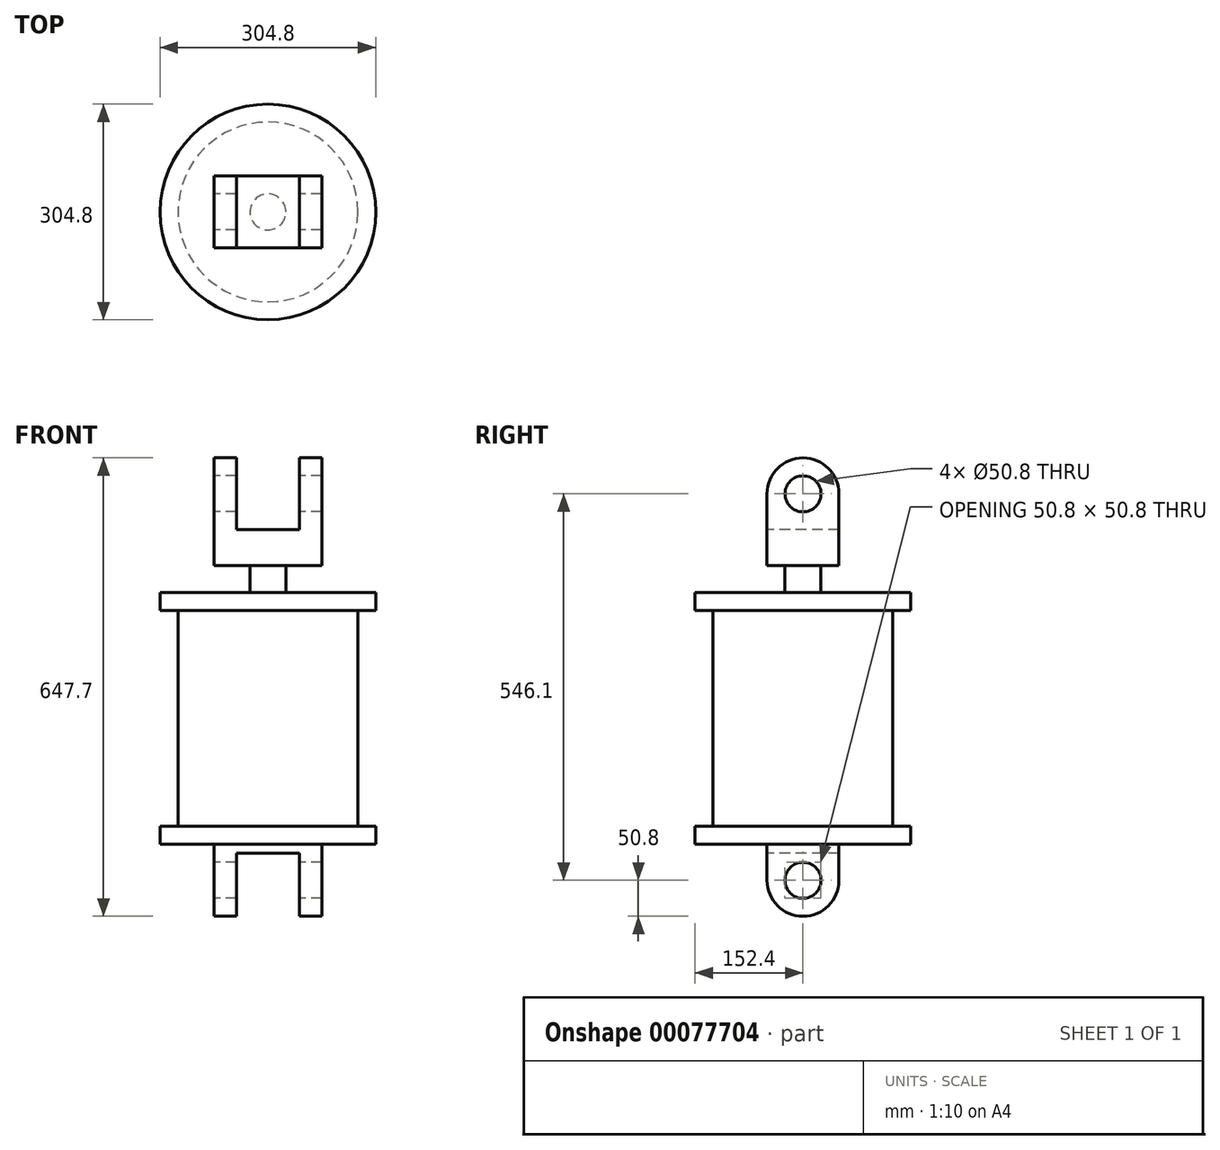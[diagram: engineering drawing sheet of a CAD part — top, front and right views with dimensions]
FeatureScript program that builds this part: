
annotation { "Feature Type Name" : "Feature", "Feature Type Description" : "" }
export const myFeature = defineFeature(function(context is Context, id is Id, definition is map)
    precondition{}
    {
        {
            var Q0;
            Q0=qCreatedBy(makeId("Right.planeOp"),FACE);
            var sketch = newSketch(context, id + "F0", { "sketchPlane" : qUnion([Q0])});
            skCircle(sketch, "E0", {"center": v(0, 0) * mm, "radius": 25.4 * mm});
            skArc(sketch, "E1", {"start": v(-50.8, 0) * mm, "mid": v(0, -50.8) * mm, "end": v(50.8, 0) * mm});
            skLineSegment(sketch, "E2", {"start": v(-50.8, 0) * mm, "end": v(-50.8, 50.8) * mm});
            skLineSegment(sketch, "E3", {"start": v(-50.8, 50.8) * mm, "end": v(50.8, 50.8) * mm});
            skLineSegment(sketch, "E4", {"start": v(50.8, 50.8) * mm, "end": v(50.8, 0) * mm});
            skSolve(sketch);
        }
        {
            var Q0;
            Q0=qSketchRegion(id+"F0",true);
            extrude(context, id + "F1", {"entities" : qUnion([Q0]), "endBound" : BoundingType.SYMMETRIC, "depth" : 152.4 * mm});
        }
        {
            var Q0;
            Q0=makeQuery(id+"F1.opExtrude","SWEPT_FACE",FACE,{"disambiguationData":[OSD([sQuery(id+"F0.wireOp",EDGE,"E2")])]});
            var sketch = newSketch(context, id + "F2", { "sketchPlane" : qUnion([Q0])});
            skLineSegment(sketch, "E5.bottom", {"start": v(-44.45, 38.1) * mm, "end": v(44.45, 38.1) * mm});
            skLineSegment(sketch, "E5.top", {"start": v(-44.45, -62.27) * mm, "end": v(44.45, -62.27) * mm});
            skLineSegment(sketch, "E5.left", {"start": v(-44.45, 38.1) * mm, "end": v(-44.45, -62.27) * mm});
            skLineSegment(sketch, "E5.right", {"start": v(44.45, 38.1) * mm, "end": v(44.45, -62.27) * mm});
            skLineSegment(sketch, "E6", {"start": v(0, 50.8) * mm, "end": v(0, -95.86) * mm, "construction": true});
            skSolve(sketch);
        }
        {
            var Q0;
            Q0=qSketchRegion(id+"F2",true);
            extrude(context, id + "F3", {"entities" : qUnion([Q0]), "operationType" : NewBodyOperationType.REMOVE, "endBound" : BoundingType.THROUGH_ALL, "oppositeDirection" : true, "depth" : 25.4 * mm});
        }
        {
            var Q0;
            Q0=makeQuery(id+"F1.opExtrude","SWEPT_FACE",FACE,{"disambiguationData":[OSD([sQuery(id+"F0.wireOp",EDGE,"E3")])]});
            var sketch = newSketch(context, id + "F4", { "sketchPlane" : qUnion([Q0])});
            skCircle(sketch, "E7", {"center": v(0, 0) * mm, "radius": 152.4 * mm});
            skSolve(sketch);
        }
        {
            var Q0;
            Q0=qSketchRegion(id+"F4",true);
            extrude(context, id + "F5", {"entities" : qUnion([Q0]), "operationType" : NewBodyOperationType.ADD, "depth" : 25.4 * mm});
        }
        {
            var Q0;
            Q0=makeQuery(id+"F5.opExtrude","CAP_FACE",FACE,{"disambiguationData":[OSD([sQuery(id+"F4.wireOp",EDGE,"E7")])],"isStart":false});
            var sketch = newSketch(context, id + "F6", { "sketchPlane" : qUnion([Q0])});
            skCircle(sketch, "E8", {"center": v(0, 0) * mm, "radius": 127 * mm});
            skSolve(sketch);
        }
        {
            var Q0;
            Q0=qSketchRegion(id+"F6",true);
            extrude(context, id + "F7", {"entities" : qUnion([Q0]), "operationType" : NewBodyOperationType.ADD, "depth" : 304.8 * mm});
        }
        {
            var Q0;
            Q0=makeQuery(id+"F7.opExtrude","CAP_FACE",FACE,{"disambiguationData":[OSD([sQuery(id+"F6.wireOp",EDGE,"E8")])],"isStart":false});
            var sketch = newSketch(context, id + "F8", { "sketchPlane" : qUnion([Q0])});
            skCircle(sketch, "E9.0", {"center": v(0, 0) * mm, "radius": 152.4 * mm});
            skSolve(sketch);
        }
        {
            var Q0;
            Q0=qSketchRegion(id+"F8",true);
            extrude(context, id + "F9", {"entities" : qUnion([Q0]), "operationType" : NewBodyOperationType.ADD, "depth" : 25.4 * mm});
        }
        {
            var Q0;
            Q0=makeQuery(id+"F9.opExtrude","CAP_FACE",FACE,{"disambiguationData":[OSD([sQuery(id+"F8.wireOp",EDGE,"E9.0")])],"isStart":false});
            var sketch = newSketch(context, id + "F10", { "sketchPlane" : qUnion([Q0])});
            skCircle(sketch, "E10", {"center": v(0, 0) * mm, "radius": 25.4 * mm});
            skSolve(sketch);
        }
        {
            var Q0;
            Q0=qSketchRegion(id+"F10",true);
            extrude(context, id + "F11", {"entities" : qUnion([Q0]), "operationType" : NewBodyOperationType.ADD, "depth" : 38.1 * mm});
        }
        {
            var Q0;
            Q0=makeQuery(id+"F11.opExtrude","CAP_FACE",FACE,{"disambiguationData":[OSD([sQuery(id+"F10.wireOp",EDGE,"E10")])],"isStart":false});
            var sketch = newSketch(context, id + "F12", { "sketchPlane" : qUnion([Q0])});
            skLineSegment(sketch, "E11.0", {"start": v(76.2, 50.8) * mm, "end": v(-76.2, 50.8) * mm});
            skLineSegment(sketch, "E12.0", {"start": v(76.2, -50.8) * mm, "end": v(76.2, 50.8) * mm});
            skLineSegment(sketch, "E13.0", {"start": v(76.2, -50.8) * mm, "end": v(-76.2, -50.8) * mm});
            skLineSegment(sketch, "E14.0", {"start": v(-76.2, -50.8) * mm, "end": v(-76.2, 50.8) * mm});
            skSolve(sketch);
        }
        {
            var Q0;
            Q0=qSketchRegion(id+"F12",true);
            extrude(context, id + "F13", {"entities" : qUnion([Q0]), "operationType" : NewBodyOperationType.ADD, "depth" : 152.4 * mm});
        }
        {
            var Q0;
            Q0=makeQuery(id+"F13.opExtrude","SWEPT_FACE",FACE,{"disambiguationData":[OSD([sQuery(id+"F12.wireOp",EDGE,"E13.0")])]});
            var sketch = newSketch(context, id + "F14", { "sketchPlane" : qUnion([Q0])});
            skLineSegment(sketch, "E15.0", {"start": v(-44.45, 769.4) * mm, "end": v(-44.45, 495.3) * mm});
            skLineSegment(sketch, "E16.0", {"start": v(44.45, 777.53) * mm, "end": v(44.45, 495.3) * mm});
            skPoint(sketch, "E17.orphan", {"position": v(-44.45, 38.1) * mm});
            skPoint(sketch, "E18.orphan", {"position": v(44.45, 38.1) * mm});
            skLineSegment(sketch, "E19.0", {"start": v(44.45, 495.3) * mm, "end": v(-44.45, 495.3) * mm});
            skLineSegment(sketch, "E20.trimOffspring", {"start": v(-44.45, 38.1) * mm, "end": v(-44.45, 0) * mm});
            skLineSegment(sketch, "E21.trimOffspring", {"start": v(44.45, 38.1) * mm, "end": v(44.45, 0) * mm});
            skLineSegment(sketch, "E22", {"start": v(-44.45, 769.4) * mm, "end": v(44.45, 777.53) * mm});
            skSolve(sketch);
        }
        {
            var Q0;
            Q0=qSketchRegion(id+"F14",true);
            extrude(context, id + "F15", {"entities" : qUnion([Q0]), "operationType" : NewBodyOperationType.REMOVE, "endBound" : BoundingType.THROUGH_ALL, "oppositeDirection" : true, "depth" : 25.4 * mm});
        }
        {
            var Q0;
            {var subQ0=sQuery(id+"F12.wireOp",EDGE,"E11.0");var subQ1=sQuery(id+"F12.wireOp",EDGE,"E14.0");Q0=makeQuery(id+"F15.boolean.opBoolean","SPLIT",EDGE,{"disambiguationData":[TD([makeQuery(id+"F13.opExtrude","SWEPT_FACE",FACE,{"disambiguationData":[OSD([subQ1])]})])],"derivedFrom":makeQuery(id+"F13.opExtrude","CAP_EDGE",EDGE,{"disambiguationData":[OSD([subQ0])],"isStart":false})});}
            var Q1;
            {var subQ0=sQuery(id+"F12.wireOp",EDGE,"E11.0");var subQ1=sQuery(id+"F12.wireOp",EDGE,"E12.0");Q1=makeQuery(id+"F15.boolean.opBoolean","SPLIT",EDGE,{"disambiguationData":[TD([makeQuery(id+"F13.opExtrude","SWEPT_FACE",FACE,{"disambiguationData":[OSD([subQ1])]})])],"derivedFrom":makeQuery(id+"F13.opExtrude","CAP_EDGE",EDGE,{"disambiguationData":[OSD([subQ0])],"isStart":false})});}
            var Q2;
            {var subQ0=sQuery(id+"F12.wireOp",EDGE,"E13.0");var subQ1=sQuery(id+"F12.wireOp",EDGE,"E12.0");Q2=makeQuery(id+"F15.boolean.opBoolean","SPLIT",EDGE,{"disambiguationData":[TD([makeQuery(id+"F13.opExtrude","SWEPT_FACE",FACE,{"disambiguationData":[OSD([subQ1])]})])],"derivedFrom":makeQuery(id+"F13.opExtrude","CAP_EDGE",EDGE,{"disambiguationData":[OSD([subQ0])],"isStart":false})});}
            var Q3;
            {var subQ0=sQuery(id+"F12.wireOp",EDGE,"E13.0");var subQ1=sQuery(id+"F12.wireOp",EDGE,"E14.0");Q3=makeQuery(id+"F15.boolean.opBoolean","SPLIT",EDGE,{"disambiguationData":[TD([makeQuery(id+"F13.opExtrude","SWEPT_FACE",FACE,{"disambiguationData":[OSD([subQ1])]})])],"derivedFrom":makeQuery(id+"F13.opExtrude","CAP_EDGE",EDGE,{"disambiguationData":[OSD([subQ0])],"isStart":false})});}
            fillet(context, id + "F16", {"entities" : qUnion([Q0, Q1, Q2, Q3]), "radius" : 50.8 * mm, "tangentPropagation" : true, "allowEdgeOverflow" : false});
        }
        {
            var Q0;
            Q0=makeQuery(id+"F13.opExtrude","SWEPT_FACE",FACE,{"disambiguationData":[OSD([sQuery(id+"F12.wireOp",EDGE,"E14.0")])]});
            var sketch = newSketch(context, id + "F17", { "sketchPlane" : qUnion([Q0])});
            skCircle(sketch, "E23", {"center": v(0, 546.1) * mm, "radius": 25.4 * mm});
            skSolve(sketch);
        }
        {
            var Q0;
            Q0=qSketchRegion(id+"F17",true);
            extrude(context, id + "F18", {"entities" : qUnion([Q0]), "operationType" : NewBodyOperationType.REMOVE, "endBound" : BoundingType.THROUGH_ALL, "oppositeDirection" : true, "depth" : 25.4 * mm});
        }
    });
